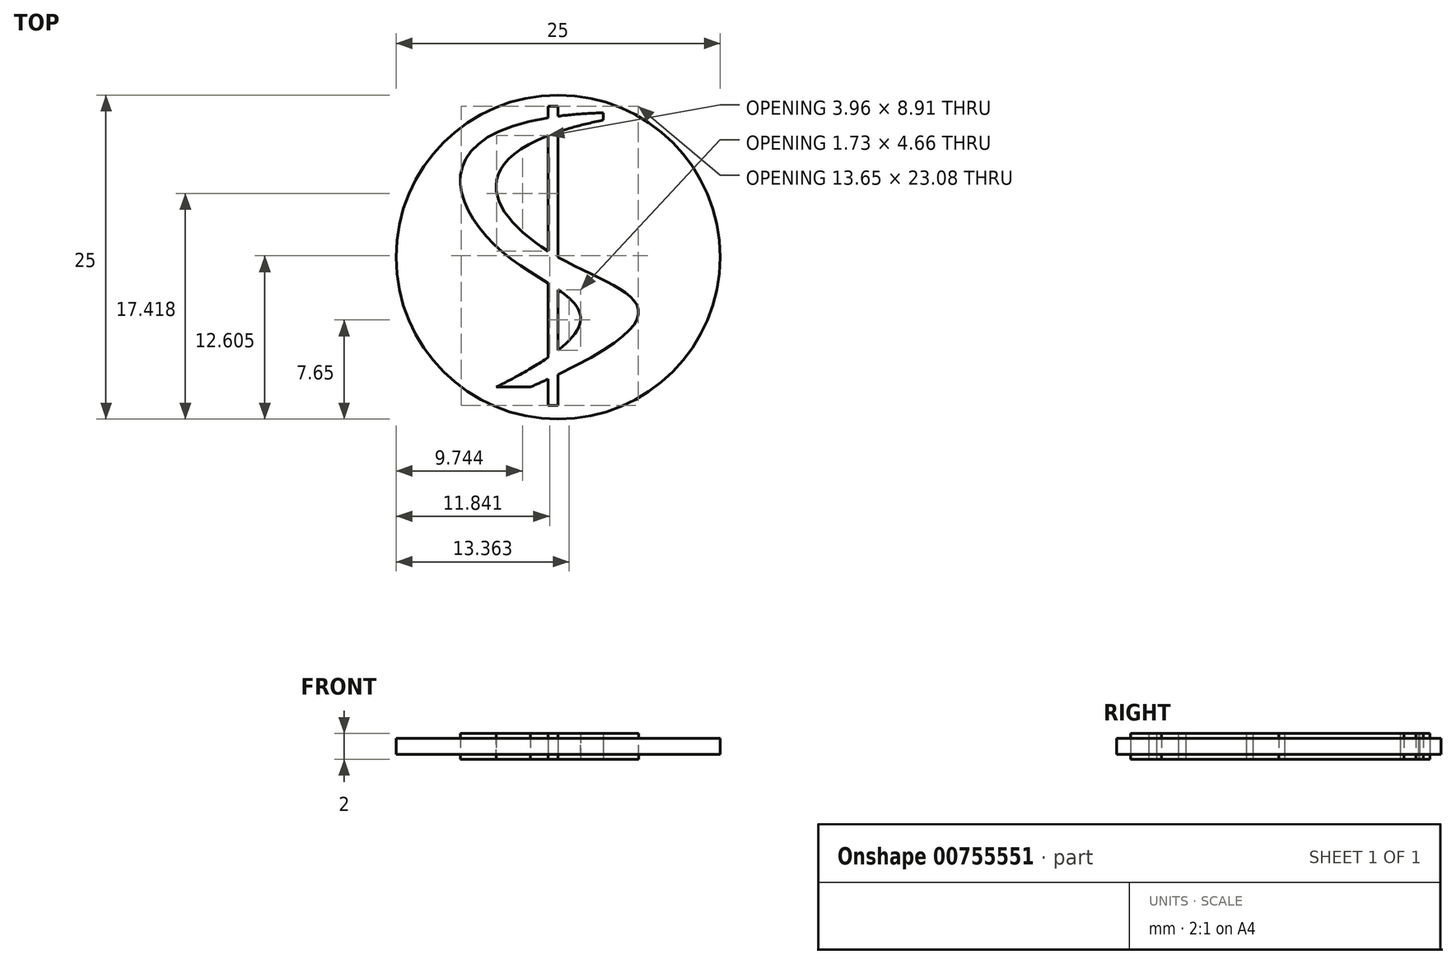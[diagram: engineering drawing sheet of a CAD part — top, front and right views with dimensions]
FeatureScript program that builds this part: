
annotation { "Feature Type Name" : "Feature", "Feature Type Description" : "" }
export const myFeature = defineFeature(function(context is Context, id is Id, definition is map)
    precondition{}
    {
        {
            var Q0;
            Q0=qCreatedBy(makeId("Top.planeOp"),FACE);
            var sketch = newSketch(context, id + "F0", { "sketchPlane" : qUnion([Q0])});
            skCircle(sketch, "E0", {"center": v(0, 0) * mm, "radius": 12.5 * mm});
            skFitSpline(sketch, "E1", {"points": [v(3.47, 10.57) * mm, v(0, 0) * mm, v(-2.12, -10.02) * mm], "startDerivative": vector(-71.2, -14.7) * mm, "endDerivative": vector(-85.93, -38.03) * mm});
            skFitSpline(sketch, "E2", {"points": [v(3.47, 11.13) * mm, v(-3.8, 0) * mm, v(-4.76, -10.02) * mm], "startDerivative": vector(-81.2, -2.36) * mm, "endDerivative": vector(-73.49, -37.17) * mm});
            skLineSegment(sketch, "E3", {"start": v(3.47, 11.13) * mm, "end": v(3.47, 10.57) * mm});
            skLineSegment(sketch, "E4", {"start": v(-4.76, -10.02) * mm, "end": v(-2.12, -10.02) * mm});
            skLineSegment(sketch, "E5.bottom", {"start": v(0, 11.65) * mm, "end": v(-0.77, 11.65) * mm});
            skLineSegment(sketch, "E5.top", {"start": v(0, -11.44) * mm, "end": v(-0.77, -11.44) * mm});
            skLineSegment(sketch, "E5.left", {"start": v(0, 11.65) * mm, "end": v(0, -11.44) * mm});
            skLineSegment(sketch, "E5.right", {"start": v(-0.77, 11.65) * mm, "end": v(-0.77, -11.44) * mm});
            skSolve(sketch);
        }
        {
            var Q0;
            Q0=makeQuery(id+"F0.imprint","IMPRINT",FACE,{"disambiguationData":[TD([[makeQuery(id+"F0.imprint","IMPRINT",EDGE,{"derivedFrom":sQuery(id+"F0.wireOp",EDGE,"E0")}),1.0]])]});
            var Q1;
            {var subQ0=sQuery(id+"F0.wireOp",EDGE,"E5.right");var subQ1=sQuery(id+"F0.wireOp",EDGE,"E1");var subQ2=makeQuery(id+"F0.imprint","INTERSECT",VERTEX,{"disambiguationData":[OD(0.0)],"derivedFrom":[subQ1,subQ0]});Q1=makeQuery(id+"F0.imprint","IMPRINT",FACE,{"disambiguationData":[TD([[makeQuery(id+"F0.imprint","IMPRINT",EDGE,{"disambiguationData":[TD([[subQ2,-1.0]])],"derivedFrom":subQ1}),1.0]])]});}
            var Q2;
            {var subQ0=sQuery(id+"F0.wireOp",EDGE,"E5.left");var subQ1=sQuery(id+"F0.wireOp",EDGE,"E2");var subQ2=makeQuery(id+"F0.imprint","INTERSECT",VERTEX,{"disambiguationData":[OD(1.0)],"derivedFrom":[subQ1,subQ0]});Q2=makeQuery(id+"F0.imprint","IMPRINT",FACE,{"disambiguationData":[TD([[makeQuery(id+"F0.imprint","IMPRINT",EDGE,{"disambiguationData":[TD([[subQ2,-1.0]])],"derivedFrom":subQ1}),-1.0]])]});}
            extrude(context, id + "F1", {"entities" : qUnion([Q0, Q1, Q2]), "endBound" : BoundingType.SYMMETRIC, "depth" : 1.25 * mm, "offsetDistance" : 25 * mm});
        }
        {
            var Q0;
            {var subQ0=sQuery(id+"F0.wireOp",EDGE,"E5.right");var subQ1=sQuery(id+"F0.wireOp",EDGE,"E1");var subQ2=makeQuery(id+"F0.imprint","INTERSECT",VERTEX,{"disambiguationData":[OD(0.0)],"derivedFrom":[subQ1,subQ0]});Q0=makeQuery(id+"F0.imprint","IMPRINT",FACE,{"disambiguationData":[TD([[makeQuery(id+"F0.imprint","IMPRINT",EDGE,{"disambiguationData":[TD([[subQ2,-1.0]])],"derivedFrom":subQ1}),-1.0]])]});}
            var Q1;
            {var subQ0=sQuery(id+"F0.wireOp",EDGE,"E5.right");var subQ1=sQuery(id+"F0.wireOp",EDGE,"E1");var subQ2=makeQuery(id+"F0.imprint","INTERSECT",VERTEX,{"disambiguationData":[OD(1.0)],"derivedFrom":[subQ1,subQ0]});Q1=makeQuery(id+"F0.imprint","IMPRINT",FACE,{"disambiguationData":[TD([[makeQuery(id+"F0.imprint","IMPRINT",EDGE,{"disambiguationData":[TD([[subQ2,-1.0]])],"derivedFrom":subQ1}),-1.0]])]});}
            var Q2;
            {var subQ5=sQuery(id+"F0.wireOp",EDGE,"E5.bottom");Q2=makeQuery(id+"F0.imprint","IMPRINT",FACE,{"disambiguationData":[TD([[makeQuery(id+"F0.imprint","IMPRINT",EDGE,{"derivedFrom":subQ5}),1.0]])]});}
            var Q3;
            {var subQ0=sQuery(id+"F0.wireOp",EDGE,"E5.left");var subQ1=sQuery(id+"F0.wireOp",EDGE,"E1");var subQ2=makeQuery(id+"F0.imprint","INTERSECT",VERTEX,{"disambiguationData":[OD(0.0)],"derivedFrom":[subQ1,subQ0]});Q3=makeQuery(id+"F0.imprint","IMPRINT",FACE,{"disambiguationData":[TD([[makeQuery(id+"F0.imprint","IMPRINT",EDGE,{"disambiguationData":[TD([[subQ2,-1.0]])],"derivedFrom":subQ1}),-1.0]])]});}
            var Q4;
            {var subQ0=sQuery(id+"F0.wireOp",EDGE,"E3");Q4=makeQuery(id+"F0.imprint","IMPRINT",FACE,{"disambiguationData":[TD([[makeQuery(id+"F0.imprint","IMPRINT",EDGE,{"derivedFrom":subQ0}),-1.0]])]});}
            var Q5;
            {var subQ0=sQuery(id+"F0.wireOp",EDGE,"E5.left");var subQ1=sQuery(id+"F0.wireOp",EDGE,"E1");var subQ2=makeQuery(id+"F0.imprint","INTERSECT",VERTEX,{"disambiguationData":[OD(0.0)],"derivedFrom":[subQ1,subQ0]});Q5=makeQuery(id+"F0.imprint","IMPRINT",FACE,{"disambiguationData":[TD([[makeQuery(id+"F0.imprint","IMPRINT",EDGE,{"disambiguationData":[TD([[subQ2,-1.0]])],"derivedFrom":subQ1}),1.0]])]});}
            var Q6;
            {var subQ0=sQuery(id+"F0.wireOp",EDGE,"E5.right");var subQ1=sQuery(id+"F0.wireOp",EDGE,"E2");var subQ2=makeQuery(id+"F0.imprint","INTERSECT",VERTEX,{"disambiguationData":[OD(1.0)],"derivedFrom":[subQ1,subQ0]});Q6=makeQuery(id+"F0.imprint","IMPRINT",FACE,{"disambiguationData":[TD([[makeQuery(id+"F0.imprint","IMPRINT",EDGE,{"disambiguationData":[TD([[subQ2,-1.0]])],"derivedFrom":subQ1}),-1.0]])]});}
            var Q7;
            {var subQ5=sQuery(id+"F0.wireOp",EDGE,"E5.top");Q7=makeQuery(id+"F0.imprint","IMPRINT",FACE,{"disambiguationData":[TD([[makeQuery(id+"F0.imprint","IMPRINT",EDGE,{"derivedFrom":subQ5}),-1.0]])]});}
            var Q8;
            {var subQ0=sQuery(id+"F0.wireOp",EDGE,"E4");Q8=makeQuery(id+"F0.imprint","IMPRINT",FACE,{"disambiguationData":[TD([[makeQuery(id+"F0.imprint","IMPRINT",EDGE,{"derivedFrom":subQ0}),1.0]])]});}
            var Q9;
            {var subQ0=sQuery(id+"F0.wireOp",EDGE,"E5.left");var subQ1=sQuery(id+"F0.wireOp",EDGE,"E1");var subQ2=makeQuery(id+"F0.imprint","INTERSECT",VERTEX,{"disambiguationData":[OD(2.0)],"derivedFrom":[subQ1,subQ0]});Q9=makeQuery(id+"F0.imprint","IMPRINT",FACE,{"disambiguationData":[TD([[makeQuery(id+"F0.imprint","IMPRINT",EDGE,{"disambiguationData":[TD([[subQ2,-1.0]])],"derivedFrom":subQ1}),-1.0]])]});}
            var Q10;
            {var subQ0=sQuery(id+"F0.wireOp",EDGE,"E5.left");var subQ1=sQuery(id+"F0.wireOp",EDGE,"E1");var subQ2=makeQuery(id+"F0.imprint","INTERSECT",VERTEX,{"disambiguationData":[OD(1.0)],"derivedFrom":[subQ1,subQ0]});Q10=makeQuery(id+"F0.imprint","IMPRINT",FACE,{"disambiguationData":[TD([[makeQuery(id+"F0.imprint","IMPRINT",EDGE,{"disambiguationData":[TD([[subQ2,-1.0]])],"derivedFrom":subQ1}),-1.0]])]});}
            extrude(context, id + "F2", {"entities" : qUnion([Q0, Q1, Q2, Q3, Q4, Q5, Q6, Q7, Q8, Q9, Q10]), "endBound" : BoundingType.SYMMETRIC, "depth" : 2 * mm, "offsetDistance" : 25 * mm});
        }
    });
